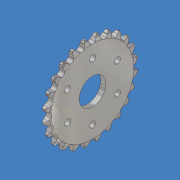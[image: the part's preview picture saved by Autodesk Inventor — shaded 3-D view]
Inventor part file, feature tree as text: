
AUTODESK INVENTOR PART (.ipt)
format: ipt  version: 2015 (Build 190159000, 159)  size: 413,184 bytes
history: native  units: mm (DEFAULTED — no unit token found)
features: sketch x4, hole x2, pattern_circular x2, other x1, extrude x1
ambient origin geometry x8: Origin, YZ Plane, XZ Plane, XY Plane, X Axis, Y Axis, Z Axis, Center Point
bodies: Solid1 (feature_tree)
feature tree (10):
  other  "Sprocket Blank"
  extrude  "Tooth Profile"  Depth=39.032279mm
  hole  "Bore"  [1 undecoded]
  pattern_circular  "Circular Pattern2"  [2 undecoded]
  hole  "Hole3"  [1 undecoded]
  pattern_circular  "Circular Pattern3"  [2 undecoded]
  sketch  "Sketch1"  dims[d0=4.276725mm d1=39.032279mm]
  sketch  "Sketch2"  dims[d2=4.7625mm d3=10.125075mm]
  sketch  "Sketch5"  dims[d4=90.0deg]
  sketch  "Sketch10"  dims[d9=72.973859mm d10=1.308997mm d11=7.00079mm d12=3.224188mm d13=0.921672mm d14=4.148835mm d15=2.474006mm d16=6.6548mm d17=5.1816mm d18=25.4mm d19=0.0mm d42=22.2123mm d43=12.7mm d44=9.525mm d45=6.35mm d46=14.3117mm d47=19.05mm d48=20.594885mm d53=240.0mm d55=360.0deg d56=23.8125mm d57=5.2324mm d58=12.7mm d59=9.525mm d60=6.35mm d61=14.3117mm d62=19.05mm d63=20.594885mm d64=60.0mm d66=360.0deg]
note: 6 required parameter values undecoded (feature->parameter linkage not recoverable at this tier; creation-order binding heuristic only, values carry confidence <= 0.55)
